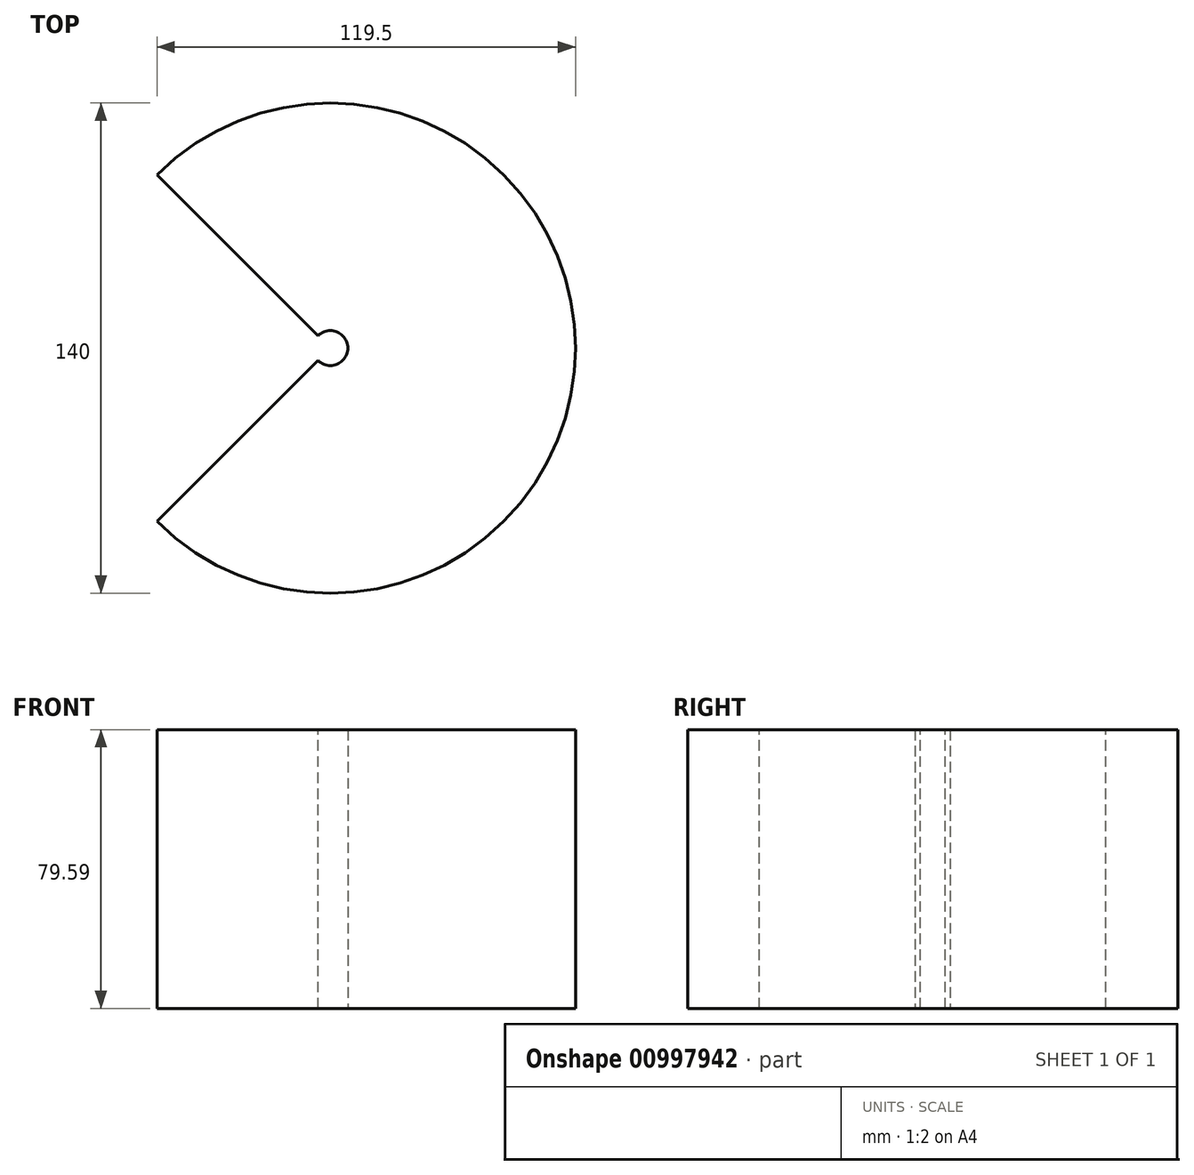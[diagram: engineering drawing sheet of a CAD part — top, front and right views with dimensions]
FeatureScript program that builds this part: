
annotation { "Feature Type Name" : "Feature", "Feature Type Description" : "" }
export const myFeature = defineFeature(function(context is Context, id is Id, definition is map)
    precondition{}
    {
        {
            var Q0;
            Q0=qCreatedBy(makeId("Front.planeOp"),FACE);
            var sketch = newSketch(context, id + "F0", { "sketchPlane" : qUnion([Q0])});
            skLineSegment(sketch, "E0", {"start": v(0, 0) * mm, "end": v(5, 0) * mm});
            skLineSegment(sketch, "E1.bottom", {"start": v(5, 0) * mm, "end": v(70, 0) * mm});
            skLineSegment(sketch, "E1.top", {"start": v(5, 79.59) * mm, "end": v(70, 79.59) * mm});
            skLineSegment(sketch, "E1.left", {"start": v(5, 0) * mm, "end": v(5, 79.59) * mm});
            skLineSegment(sketch, "E1.right", {"start": v(70, 0) * mm, "end": v(70, 79.59) * mm});
            skLineSegment(sketch, "E2", {"start": v(0, 0) * mm, "end": v(0, 79.83) * mm, "construction": true});
            skSolve(sketch);
        }
        {
            var Q0;
            Q0=makeQuery(id+"F0.imprint","IMPRINT",FACE,{"disambiguationData":[TD([[makeQuery(id+"F0.imprint","IMPRINT",EDGE,{"derivedFrom":sQuery(id+"F0.wireOp",EDGE,"E1.bottom")}),1.0]])]});
            var Q1;
            Q1=sQuery(id+"F0.wireOp",EDGE,"E2");
            revolve(context, id + "F1", {"surfaceOperationType" : NewSurfaceOperationType.NEW, "entities" : qUnion([Q0]), "axis" : qUnion([Q1]), "revolveType" : RevolveType.SYMMETRIC, "angle" : 270 * degree});
        }
    });
